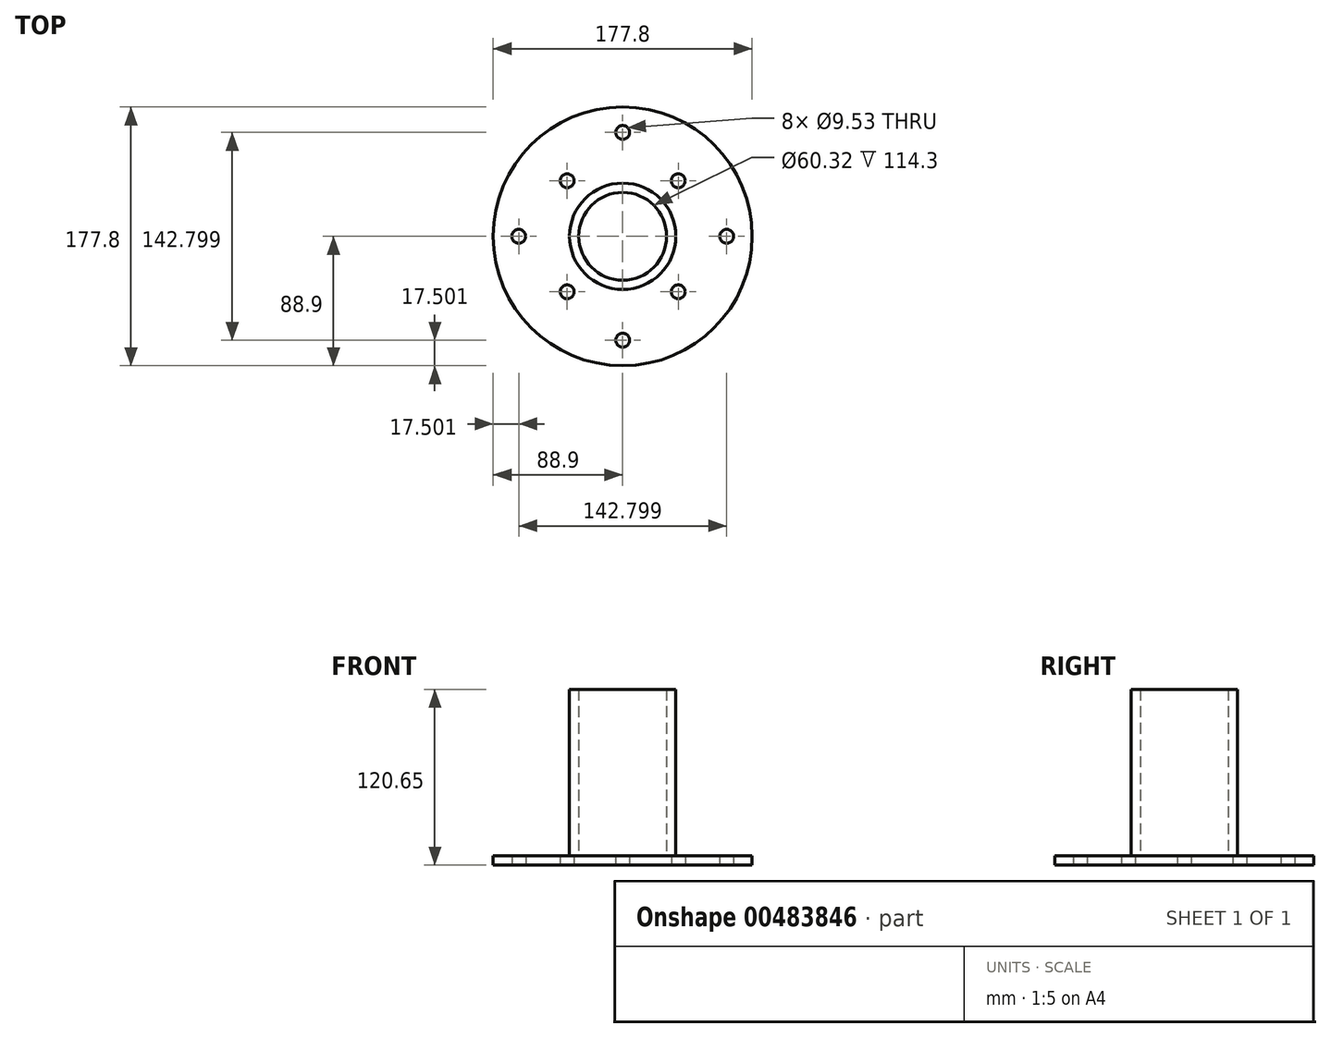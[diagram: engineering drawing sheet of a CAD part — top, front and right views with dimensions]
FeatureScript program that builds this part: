
annotation { "Feature Type Name" : "Feature", "Feature Type Description" : "" }
export const myFeature = defineFeature(function(context is Context, id is Id, definition is map)
    precondition{}
    {
        {
            var Q0;
            Q0=qCreatedBy(makeId("Top.planeOp"),FACE);
            var sketch = newSketch(context, id + "F0", { "sketchPlane" : qUnion([Q0])});
            skCircle(sketch, "E0", {"center": v(0, 0) * mm, "radius": 88.9 * mm});
            skCircle(sketch, "E1", {"center": v(0, 71.4) * mm, "radius": 4.76 * mm});
            skCircle(sketch, "E2.1.0", {"center": v(-71.4, 0) * mm, "radius": 4.76 * mm});
            skCircle(sketch, "E2.2.0", {"center": v(0, -71.4) * mm, "radius": 4.76 * mm});
            skCircle(sketch, "E2.3.0", {"center": v(71.4, 0) * mm, "radius": 4.76 * mm});
            skCircle(sketch, "E3", {"center": v(-38.15, -38.15) * mm, "radius": 4.76 * mm});
            skCircle(sketch, "E4.1.0", {"center": v(38.15, -38.15) * mm, "radius": 4.76 * mm});
            skCircle(sketch, "E4.2.0", {"center": v(38.15, 38.15) * mm, "radius": 4.76 * mm});
            skCircle(sketch, "E4.3.0", {"center": v(-38.15, 38.15) * mm, "radius": 4.76 * mm});
            skSolve(sketch);
        }
        {
            var Q0;
            Q0 = qSketchRegion(id + "F0", true);
            extrude(context, id + "F1", {"entities" : qUnion([Q0]), "depth" : 6.35 * mm});
        }
        {
            var Q0;
            Q0=makeQuery(id+"F1.opExtrude","CAP_FACE",FACE,{"disambiguationData":[OSD([sQuery(id+"F0.wireOp",EDGE,"E0"),sQuery(id+"F0.wireOp",EDGE,"E1"),sQuery(id+"F0.wireOp",EDGE,"E2.1.0"),sQuery(id+"F0.wireOp",EDGE,"E2.2.0"),sQuery(id+"F0.wireOp",EDGE,"E2.3.0"),sQuery(id+"F0.wireOp",EDGE,"E3"),sQuery(id+"F0.wireOp",EDGE,"E4.1.0"),sQuery(id+"F0.wireOp",EDGE,"E4.2.0"),sQuery(id+"F0.wireOp",EDGE,"E4.3.0")])],"isStart":false});
            var sketch = newSketch(context, id + "F2", { "sketchPlane" : qUnion([Q0])});
            skCircle(sketch, "E5", {"center": v(0, 0) * mm, "radius": 36.51 * mm});
            skCircle(sketch, "E6", {"center": v(0, 0) * mm, "radius": 30.16 * mm});
            skSolve(sketch);
        }
        {
            var Q0;
            Q0=makeQuery(id+"F2.imprint","IMPRINT",FACE,{"disambiguationData":[TD([[makeQuery(id+"F2.imprint","IMPRINT",EDGE,{"derivedFrom":sQuery(id+"F2.wireOp",EDGE,"E5")}),1.0]])]});
            extrude(context, id + "F3", {"entities" : qUnion([Q0]), "operationType" : NewBodyOperationType.ADD, "depth" : 114.3 * mm});
        }
        {
            var Q0;
            {var subQ0=sQuery(id+"F0.wireOp",EDGE,"E2.1.0");var subQ1=sQuery(id+"F0.wireOp",EDGE,"E1");var subQ2=sQuery(id+"F0.wireOp",EDGE,"E2.2.0");var subQ3=sQuery(id+"F0.wireOp",EDGE,"E0");var subQ4=sQuery(id+"F0.wireOp",EDGE,"E2.3.0");var subQ5=sQuery(id+"F0.wireOp",EDGE,"E3");var subQ6=sQuery(id+"F0.wireOp",EDGE,"E4.1.0");var subQ7=sQuery(id+"F0.wireOp",EDGE,"E4.2.0");var subQ8=sQuery(id+"F0.wireOp",EDGE,"E4.3.0");Q0=makeQuery(id+"F3.boolean.opBoolean","SPLIT",FACE,{"disambiguationData":[TD([makeQuery(id+"F1.opExtrude","SWEPT_FACE",FACE,{"disambiguationData":[OSD([subQ3])]})])],"derivedFrom":makeQuery(id+"F1.opExtrude","CAP_FACE",FACE,{"disambiguationData":[OSD([subQ3,subQ1,subQ0,subQ2,subQ4,subQ5,subQ6,subQ7,subQ8])],"isStart":false})});}
            var sketch = newSketch(context, id + "F4", { "sketchPlane" : qUnion([Q0])});
            skLineSegment(sketch, "E7", {"start": v(33.1, 82.5) * mm, "end": v(13.6, 33.89) * mm});
            skSolve(sketch);
        }
        {
            var Q0;
            Q0=sQuery(id+"F4.wireOp",EDGE,"E7");
            cPlane(context, id + "F5", {"entities" : qUnion([Q0]), "cplaneType" : CPlaneType.LINE_ANGLE, "offset" : 25.4 * mm, "angle" : 90 * degree, "oppositeDirection" : true, "width" : 152.4 * mm, "height" : 152.4 * mm});
        }
    });
